# Revit family: TBW01407A_TAC
name_source: partatom
category: Plumbing Fixtures
revit_build: Autodesk Revit 2018 (Build: 20170223_1515(x64)
units: mm (PartAtom-declared; Revit-internal decimal feet)

## family parameters
Always vertical = Yes
Cut with Voids When Loaded = No
OmniClass Number = 23.45.00.00
OmniClass Title = Sanitary, Laundry, and Cleaning Equipment
Part Type = Normal
Room Calculation Point = No
Round Connector Dimension = Use Diameter
Shared = No
Work Plane-Based = No

## types (1)
- TBW01407A_TAC
    CW Connection = Yes
    Description = Thermostat Shower Column with Over Head Shower(2 mode)
    Finish = Polished Chrome
    HW Connection = Yes
    Height = 1190 mm  [stored 3.9042 ft]
    Length = 586 mm
    Manufacturer = TOTO LTD.
    Material = <By Category>
    Model = TBW01407A
    URL = https://asia.toto.com
    Vent Connection = No
    Waste Connection = No
    Water Pressure = 0.05~1.0MPa
    Width = 298 mm  [stored 0.97769 ft]

note: [stored X ft] marks values corroborated as IEEE doubles in the binary element streams (Revit-internal decimal feet)

## geometry (parser evidence)
native form markers: Sweep x2
no freeform markers — native parametric forms only
